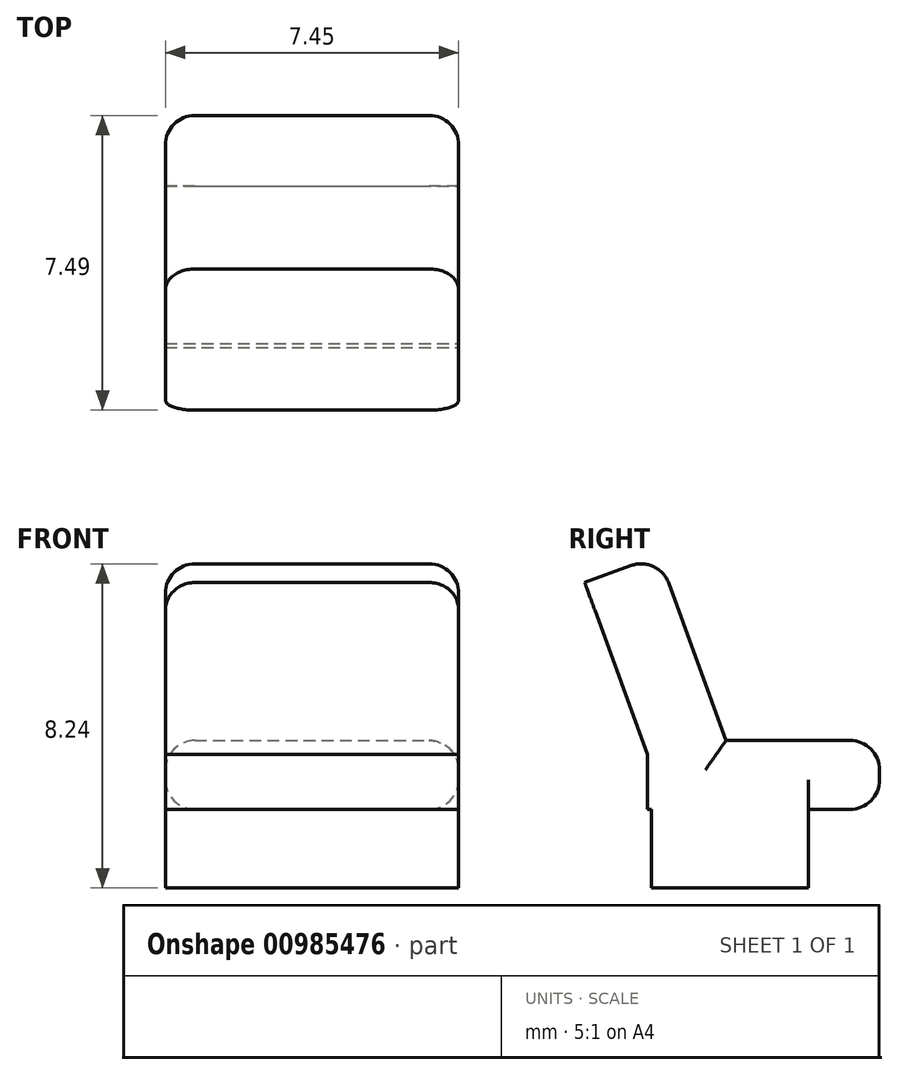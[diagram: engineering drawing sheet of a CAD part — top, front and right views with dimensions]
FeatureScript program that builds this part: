
annotation { "Feature Type Name" : "Feature", "Feature Type Description" : "" }
export const myFeature = defineFeature(function(context is Context, id is Id, definition is map)
    precondition{}
    {
        {
            var Q0;
            Q0=qCreatedBy(makeId("Top.planeOp"),FACE);
            var sketch = newSketch(context, id + "F0", { "sketchPlane" : qUnion([Q0])});
            skLineSegment(sketch, "E0.bottom", {"start": v(0, 0) * mm, "end": v(7.45, 0) * mm});
            skLineSegment(sketch, "E0.top", {"start": v(0, 4) * mm, "end": v(7.45, 4) * mm});
            skLineSegment(sketch, "E0.left", {"start": v(0, 0) * mm, "end": v(0, 4) * mm});
            skLineSegment(sketch, "E0.right", {"start": v(7.45, 0) * mm, "end": v(7.45, 4) * mm});
            skSolve(sketch);
        }
        {
            var Q0;
            Q0=qSketchRegion(id+"F0",true);
            extrude(context, id + "F1", {"entities" : qUnion([Q0]), "depth" : 2 * mm});
        }
        {
            var Q0;
            Q0=makeQuery(id+"F1.opExtrude","CAP_FACE",FACE,{"disambiguationData":[OSD([sQuery(id+"F0.wireOp",EDGE,"E0.bottom"),sQuery(id+"F0.wireOp",EDGE,"E0.top"),sQuery(id+"F0.wireOp",EDGE,"E0.left"),sQuery(id+"F0.wireOp",EDGE,"E0.right")])],"isStart":false});
            var sketch = newSketch(context, id + "F2", { "sketchPlane" : qUnion([Q0])});
            skLineSegment(sketch, "E1.bottom", {"start": v(0, 5.8) * mm, "end": v(7.45, 5.8) * mm});
            skLineSegment(sketch, "E1.top", {"start": v(0, -0.1) * mm, "end": v(7.45, -0.1) * mm});
            skLineSegment(sketch, "E1.left", {"start": v(0, 5.8) * mm, "end": v(0, -0.1) * mm});
            skLineSegment(sketch, "E1.right", {"start": v(7.45, 5.8) * mm, "end": v(7.45, -0.1) * mm});
            skSolve(sketch);
        }
        {
            var Q0;
            Q0=qSketchRegion(id+"F2",true);
            extrude(context, id + "F3", {"entities" : qUnion([Q0]), "operationType" : NewBodyOperationType.ADD, "depth" : 1.75 * mm});
        }
        {
            var Q0;
            Q0=makeQuery(id+"F3.opExtrude","CAP_FACE",FACE,{"disambiguationData":[OSD([sQuery(id+"F2.wireOp",EDGE,"E1.bottom"),sQuery(id+"F2.wireOp",EDGE,"E1.top"),sQuery(id+"F2.wireOp",EDGE,"E1.left"),sQuery(id+"F2.wireOp",EDGE,"E1.right")])],"isStart":false});
            var sketch = newSketch(context, id + "F4", { "sketchPlane" : qUnion([Q0])});
            skLineSegment(sketch, "E2", {"start": v(0, 1.9) * mm, "end": v(7.45, 1.9) * mm, "construction": true});
            skSolve(sketch);
        }
        {
            var Q0;
            Q0=sQuery(id+"F4.wireOp",EDGE,"E2");
            cPlane(context, id + "F5", {"entities" : qUnion([Q0]), "cplaneType" : CPlaneType.LINE_ANGLE, "offset" : 25 * mm, "angle" : 20 * degree, "width" : 150 * mm, "height" : 150 * mm});
        }
        {
            var Q0;
            Q0=qCreatedBy(id+"F5.planeOp",FACE);
            var sketch = newSketch(context, id + "F6", { "sketchPlane" : qUnion([Q0])});
            skLineSegment(sketch, "E3.bottom", {"start": v(0, 2.87) * mm, "end": v(-7.45, 2.87) * mm});
            skLineSegment(sketch, "E3.top", {"start": v(0, 7.87) * mm, "end": v(-7.45, 7.87) * mm});
            skLineSegment(sketch, "E3.left", {"start": v(0, 2.87) * mm, "end": v(0, 7.87) * mm});
            skLineSegment(sketch, "E3.right", {"start": v(-7.45, 2.87) * mm, "end": v(-7.45, 7.87) * mm});
            skSolve(sketch);
        }
        {
            var Q0;
            Q0=qSketchRegion(id+"F6",true);
            extrude(context, id + "F7", {"entities" : qUnion([Q0]), "operationType" : NewBodyOperationType.ADD, "oppositeDirection" : true, "depth" : 2 * mm});
        }
        {
            var Q0;
            Q0=makeQuery(id+"F3.opExtrude","SWEPT_EDGE",EDGE,{"disambiguationData":[OSD([sQuery(id+"F2.wireOp",EDGE,"E1.bottom"),sQuery(id+"F2.wireOp",EDGE,"E1.right")])]});
            var Q1;
            Q1=makeQuery(id+"F3.opExtrude","CAP_EDGE",EDGE,{"disambiguationData":[OSD([sQuery(id+"F2.wireOp",EDGE,"E1.right")])],"isStart":false});
            var Q2;
            Q2=makeQuery(id+"F3.opExtrude","CAP_EDGE",EDGE,{"disambiguationData":[OSD([sQuery(id+"F2.wireOp",EDGE,"E1.bottom")])],"isStart":false});
            var Q3;
            Q3=makeQuery(id+"F3.opExtrude","CAP_EDGE",EDGE,{"disambiguationData":[OSD([sQuery(id+"F2.wireOp",EDGE,"E1.bottom")])],"isStart":true});
            var Q4;
            Q4=makeQuery(id+"F3.opExtrude","SWEPT_EDGE",EDGE,{"disambiguationData":[OSD([sQuery(id+"F2.wireOp",EDGE,"E1.bottom"),sQuery(id+"F2.wireOp",EDGE,"E1.left")])]});
            var Q5;
            Q5=makeQuery(id+"F3.opExtrude","CAP_EDGE",EDGE,{"disambiguationData":[OSD([sQuery(id+"F2.wireOp",EDGE,"E1.left")])],"isStart":false});
            var Q6;
            {var subQ0=sQuery(id+"F2.wireOp",EDGE,"E1.left");Q6=makeQuery(id+"F3.boolean.opBoolean","SPLIT",EDGE,{"disambiguationData":[TD([makeQuery(id+"F1.opExtrude","SWEPT_FACE",FACE,{"disambiguationData":[OSD([sQuery(id+"F0.wireOp",EDGE,"E0.top")])]})])],"derivedFrom":makeQuery(id+"F3.opExtrude","CAP_EDGE",EDGE,{"disambiguationData":[OSD([subQ0])],"isStart":true})});}
            var Q7;
            Q7=makeQuery(id+"F7.opExtrude","CAP_EDGE",EDGE,{"disambiguationData":[OSD([sQuery(id+"F6.wireOp",EDGE,"E3.left")])],"isStart":true});
            var Q8;
            Q8=makeQuery(id+"F7.opExtrude","CAP_EDGE",EDGE,{"disambiguationData":[OSD([sQuery(id+"F6.wireOp",EDGE,"E3.top")])],"isStart":true});
            var Q9;
            Q9=makeQuery(id+"F7.opExtrude","CAP_EDGE",EDGE,{"disambiguationData":[OSD([sQuery(id+"F6.wireOp",EDGE,"E3.right")])],"isStart":true});
            var Q10;
            Q10=makeQuery(id+"F7.opExtrude","SWEPT_EDGE",EDGE,{"disambiguationData":[OSD([sQuery(id+"F6.wireOp",EDGE,"E3.top"),sQuery(id+"F6.wireOp",EDGE,"E3.right")])]});
            var Q11;
            Q11=makeQuery(id+"F7.opExtrude","SWEPT_EDGE",EDGE,{"disambiguationData":[OSD([sQuery(id+"F6.wireOp",EDGE,"E3.top"),sQuery(id+"F6.wireOp",EDGE,"E3.left")])]});
            fillet(context, id + "F8", {"entities" : qUnion([Q0, Q1, Q2, Q3, Q4, Q5, Q6, Q7, Q8, Q9, Q10, Q11]), "radius" : .75 * mm, "tangentPropagation" : true, "allowEdgeOverflow" : false});
        }
        {
            var Q0;
            {var subQ0=sQuery(id+"F2.wireOp",EDGE,"E1.bottom");Q0=makeQuery(id+"F8.opFillet","BLEND_EDGE",EDGE,{"blendedFrom":[makeQuery(id+"F3.opExtrude","SWEPT_EDGE",EDGE,{"disambiguationData":[OSD([subQ0,sQuery(id+"F2.wireOp",EDGE,"E1.right")])]}),makeQuery(id+"F3.opExtrude","CAP_EDGE",EDGE,{"disambiguationData":[OSD([subQ0])],"isStart":true})],"blendedInto":[]});}
            fillet(context, id + "F9", {"entities" : qUnion([Q0]), "radius" : .75 * mm, "tangentPropagation" : true, "allowEdgeOverflow" : false});
        }
    });
